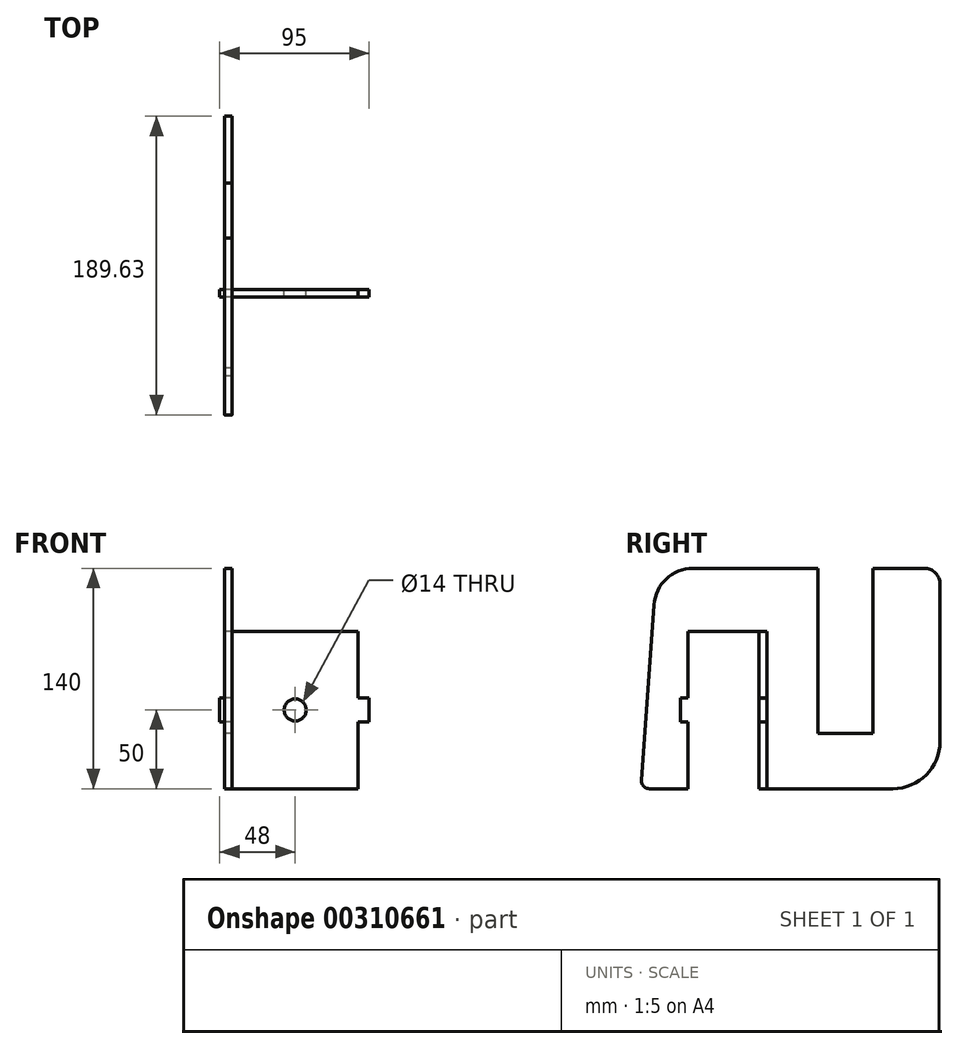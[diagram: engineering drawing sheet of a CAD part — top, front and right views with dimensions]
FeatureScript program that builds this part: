
annotation { "Feature Type Name" : "Feature", "Feature Type Description" : "" }
export const myFeature = defineFeature(function(context is Context, id is Id, definition is map)
    precondition{}
    {
        {
            var Q0;
            Q0=qCreatedBy(makeId("Right.planeOp"),FACE);
            var sketch = newSketch(context, id + "F0", { "sketchPlane" : qUnion([Q0])});
            skLineSegment(sketch, "E0.bottom", {"start": v(0, 0) * mm, "end": v(50, 0) * mm, "construction": true});
            skLineSegment(sketch, "E0.top", {"start": v(0, -105) * mm, "end": v(50, -105) * mm, "construction": true});
            skLineSegment(sketch, "E0.left", {"start": v(0, 0) * mm, "end": v(0, -105) * mm, "construction": true});
            skLineSegment(sketch, "E0.right", {"start": v(50, 0) * mm, "end": v(50, -105) * mm, "construction": true});
            skLineSegment(sketch, "E1", {"start": v(7.5, 0) * mm, "end": v(7.5, -105) * mm});
            skLineSegment(sketch, "E2", {"start": v(7.5, -105) * mm, "end": v(42.5, -105) * mm});
            skLineSegment(sketch, "E3", {"start": v(42.5, -105) * mm, "end": v(42.5, 0) * mm});
            skLineSegment(sketch, "E4", {"start": v(42.5, 0) * mm, "end": v(75, 0) * mm});
            skLineSegment(sketch, "E5", {"start": v(85, -10) * mm, "end": v(85, -110) * mm});
            skLineSegment(sketch, "E6", {"start": v(55, -140) * mm, "end": v(-30, -140) * mm});
            skLineSegment(sketch, "E7", {"start": v(-30, -140) * mm, "end": v(-30, -97.55) * mm});
            skLineSegment(sketch, "E8", {"start": v(-30, -40) * mm, "end": v(-75, -40) * mm});
            skLineSegment(sketch, "E9", {"start": v(-75, -40) * mm, "end": v(-75, -82.45) * mm});
            skLineSegment(sketch, "E10", {"start": v(-75, -140) * mm, "end": v(-99.63, -140) * mm});
            skLineSegment(sketch, "E11", {"start": v(-104.62, -134.64) * mm, "end": v(-96.66, -23.22) * mm});
            skLineSegment(sketch, "E12", {"start": v(-71.72, 0) * mm, "end": v(0, 0) * mm});
            skLineSegment(sketch, "E13.bottom", {"start": v(-75, -82.45) * mm, "end": v(-80, -82.45) * mm});
            skLineSegment(sketch, "E13.top", {"start": v(-75, -97.55) * mm, "end": v(-80, -97.55) * mm});
            skLineSegment(sketch, "E13.right", {"start": v(-80, -82.45) * mm, "end": v(-80, -97.55) * mm});
            skLineSegment(sketch, "E14.bottom", {"start": v(-30, -82.45) * mm, "end": v(-25, -82.45) * mm});
            skLineSegment(sketch, "E14.top", {"start": v(-30, -97.55) * mm, "end": v(-25, -97.55) * mm});
            skLineSegment(sketch, "E14.right", {"start": v(-25, -82.45) * mm, "end": v(-25, -97.55) * mm});
            skPoint(sketch, "E15", {"position": v(-75, -90) * mm});
            skPoint(sketch, "E16", {"position": v(-30, -90) * mm});
            skLineSegment(sketch, "E17.trimOffspring", {"start": v(-75, -97.55) * mm, "end": v(-75, -140) * mm});
            skLineSegment(sketch, "E18.trimOffspring", {"start": v(-30, -82.45) * mm, "end": v(-30, -40) * mm});
            skLineSegment(sketch, "E19", {"start": v(-71.72, 0) * mm, "end": v(7.5, 0) * mm});
            skPoint(sketch, "E20.visualSharp", {"position": v(85, -140) * mm});
            skArc(sketch, "E20.filletArc", {"start": v(55, -140) * mm, "mid": v(76.21, -131.21) * mm, "end": v(85, -110) * mm});
            skPoint(sketch, "E21.visualSharp", {"position": v(85, 0) * mm});
            skArc(sketch, "E21.filletArc", {"start": v(85, -10) * mm, "mid": v(82.07, -2.93) * mm, "end": v(75, 0) * mm});
            skPoint(sketch, "E22.visualSharp", {"position": v(-95, 0) * mm});
            skArc(sketch, "E22.filletArc", {"start": v(-71.72, 0) * mm, "mid": v(-88.76, -6.7) * mm, "end": v(-96.66, -23.22) * mm});
            skPoint(sketch, "E23.visualSharp", {"position": v(-105, -140) * mm});
            skArc(sketch, "E23.filletArc", {"start": v(-104.62, -134.64) * mm, "mid": v(-103.29, -138.4) * mm, "end": v(-99.63, -140) * mm});
            skSolve(sketch);
        }
        {
            var Q0;
            Q0 = qSketchRegion(id + "F0", true);
            extrude(context, id + "F1", {"entities" : qUnion([Q0]), "depth" : 5 * mm});
        }
        {
            var Q0;
            Q0=makeQuery(id+"F1.opExtrude","SWEPT_FACE",FACE,{"disambiguationData":[OSD([sQuery(id+"F0.wireOp",EDGE,"E14.right")])]});
            var sketch = newSketch(context, id + "F2", { "sketchPlane" : qUnion([Q0])});
            skLineSegment(sketch, "E24.bottom", {"start": v(5, -40) * mm, "end": v(85, -40) * mm});
            skLineSegment(sketch, "E24.top", {"start": v(5, -140) * mm, "end": v(85, -140) * mm});
            skLineSegment(sketch, "E24.left", {"start": v(5, -40) * mm, "end": v(5, -140) * mm});
            skLineSegment(sketch, "E24.right", {"start": v(85, -40) * mm, "end": v(85, -140) * mm});
            skLineSegment(sketch, "E25.bottom", {"start": v(5, -82.5) * mm, "end": v(-3, -82.5) * mm});
            skLineSegment(sketch, "E25.top", {"start": v(5, -97.5) * mm, "end": v(-3, -97.5) * mm});
            skLineSegment(sketch, "E25.left", {"start": v(5, -82.5) * mm, "end": v(5, -97.5) * mm});
            skLineSegment(sketch, "E25.right", {"start": v(-3, -82.5) * mm, "end": v(-3, -97.5) * mm});
            skLineSegment(sketch, "E26.bottom", {"start": v(85, -82.5) * mm, "end": v(92, -82.5) * mm});
            skLineSegment(sketch, "E26.top", {"start": v(85, -97.5) * mm, "end": v(92, -97.5) * mm});
            skLineSegment(sketch, "E26.left", {"start": v(85, -82.5) * mm, "end": v(85, -97.5) * mm});
            skLineSegment(sketch, "E26.right", {"start": v(92, -82.5) * mm, "end": v(92, -97.5) * mm});
            skCircle(sketch, "E27", {"center": v(45, -90) * mm, "radius": 7 * mm});
            skPoint(sketch, "E28", {"position": v(45, -40) * mm});
            skPoint(sketch, "E29", {"position": v(85, -90) * mm});
            skSolve(sketch);
        }
        {
            var Q0;
            Q0 = qSketchRegion(id + "F2", true);
            extrude(context, id + "F3", {"entities" : qUnion([Q0]), "depth" : 5 * mm});
        }
    });
